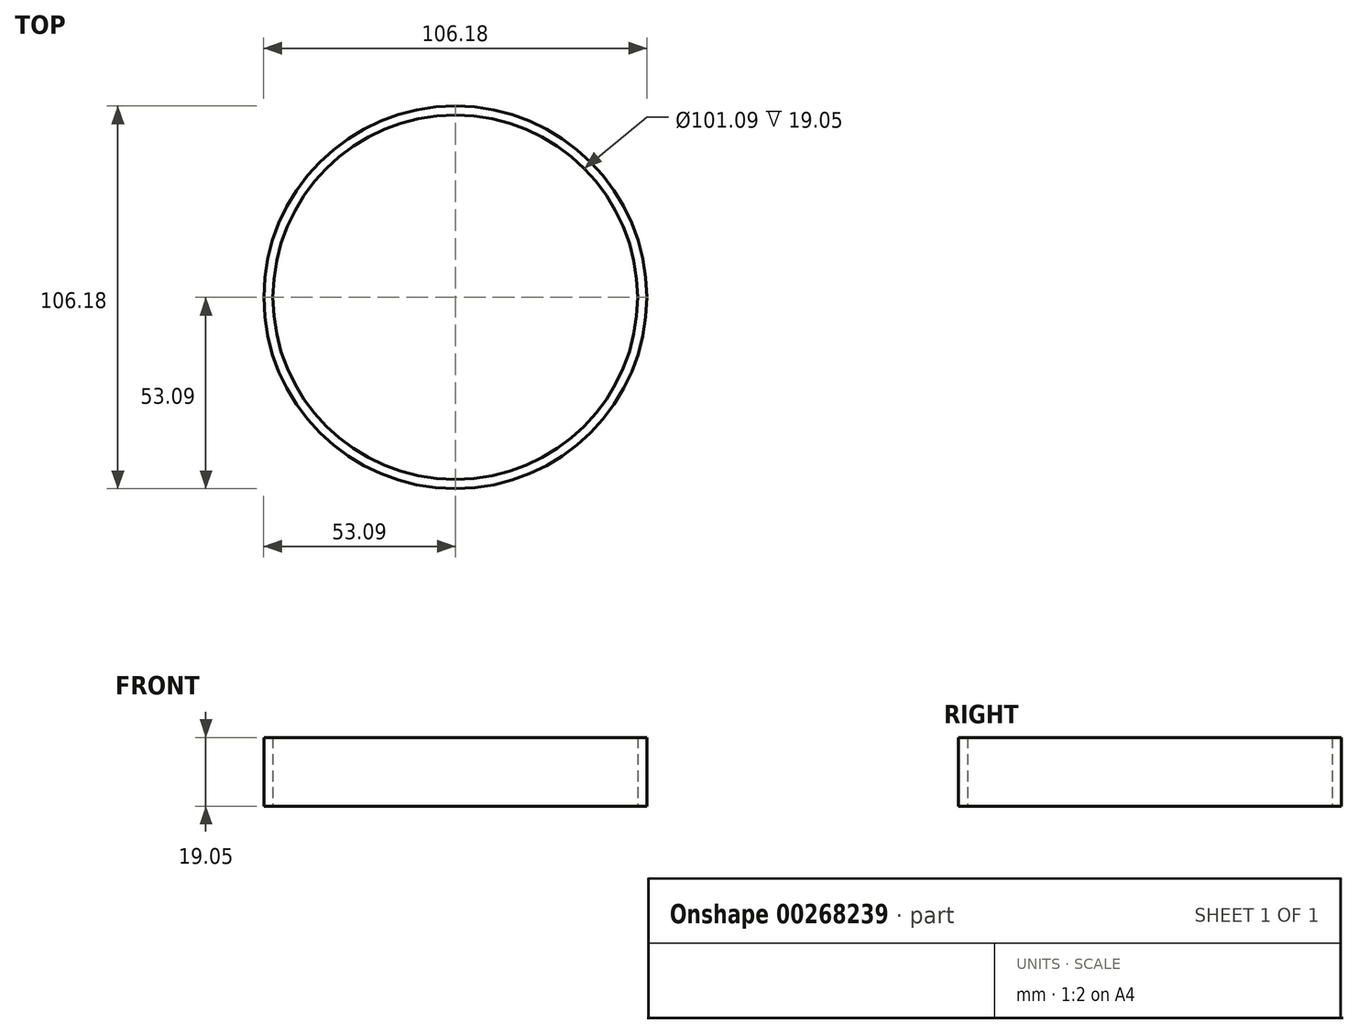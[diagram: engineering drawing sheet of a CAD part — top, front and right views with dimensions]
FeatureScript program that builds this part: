
annotation { "Feature Type Name" : "Feature", "Feature Type Description" : "" }
export const myFeature = defineFeature(function(context is Context, id is Id, definition is map)
    precondition{}
    {
        {
            var Q0;
            Q0=qCreatedBy(makeId("Top.planeOp"),FACE);
            var sketch = newSketch(context, id + "F0", { "sketchPlane" : qUnion([Q0])});
            skCircle(sketch, "E0", {"center": v(0, 0) * mm, "radius": 53.09 * mm});
            skCircle(sketch, "E1", {"center": v(0, 0) * mm, "radius": 50.55 * mm});
            skSolve(sketch);
        }
        {
            var Q0;
            Q0=makeQuery(id+"F0.imprint","IMPRINT",FACE,{"disambiguationData":[TD([[makeQuery(id+"F0.imprint","IMPRINT",EDGE,{"derivedFrom":sQuery(id+"F0.wireOp",EDGE,"E0")}),1.0]])]});
            extrude(context, id + "F1", {"entities" : qUnion([Q0]), "depth" : 19.05 * mm});
        }
    });
